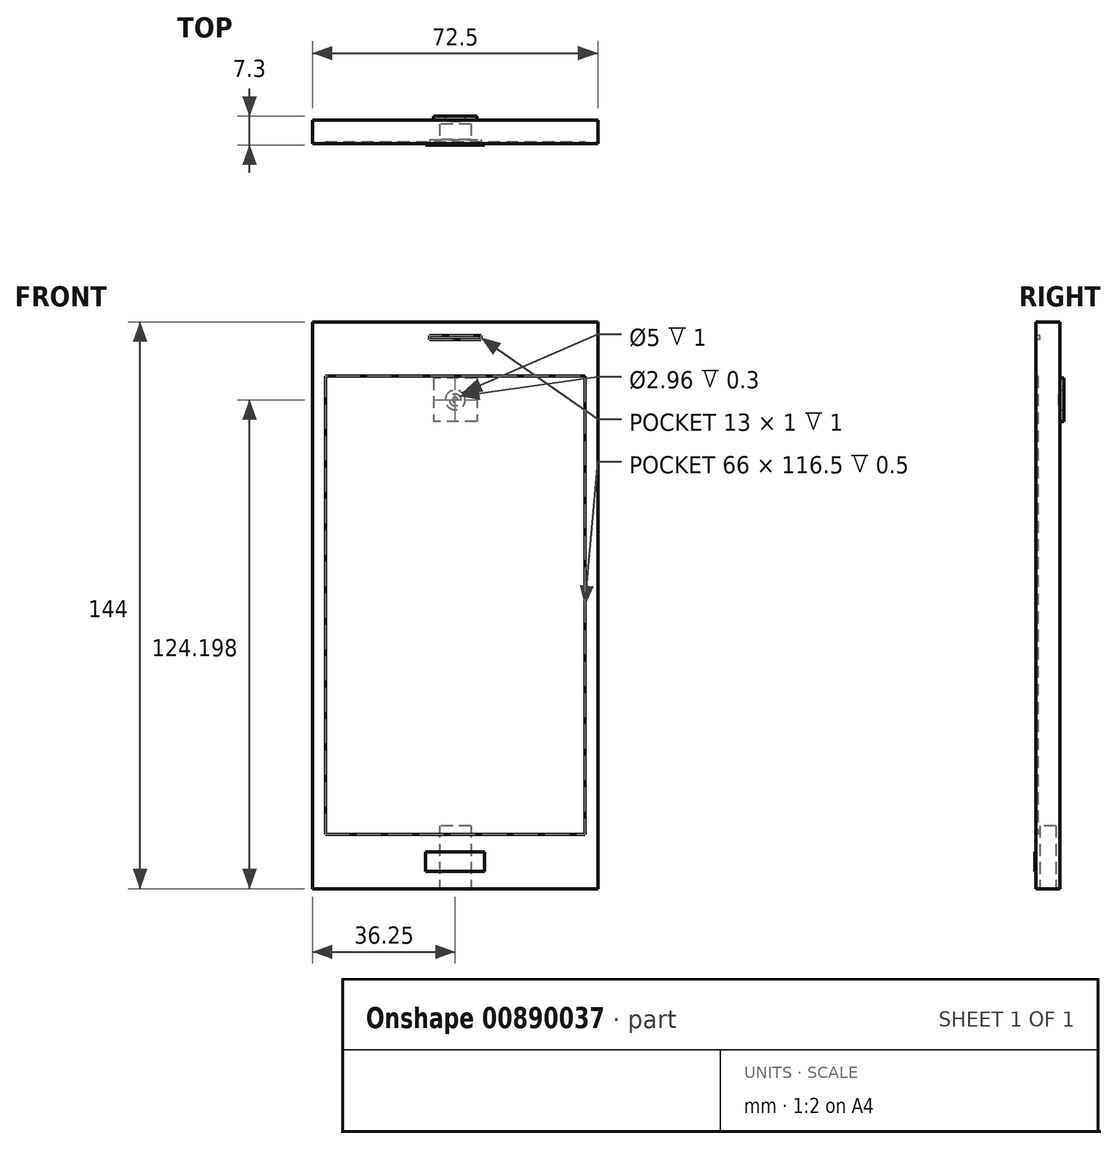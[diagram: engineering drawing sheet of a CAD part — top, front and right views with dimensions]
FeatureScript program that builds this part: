
annotation { "Feature Type Name" : "Feature", "Feature Type Description" : "" }
export const myFeature = defineFeature(function(context is Context, id is Id, definition is map)
    precondition{}
    {
        {
            var Q0;
            Q0=qCreatedBy(makeId("Front.planeOp"),FACE);
            var sketch = newSketch(context, id + "F0", { "sketchPlane" : qUnion([Q0])});
            skLineSegment(sketch, "E0.bottom", {"start": v(-36.25, 72) * mm, "end": v(36.25, 72) * mm});
            skLineSegment(sketch, "E0.top", {"start": v(-36.25, -72) * mm, "end": v(36.25, -72) * mm});
            skLineSegment(sketch, "E0.left", {"start": v(-36.25, 72) * mm, "end": v(-36.25, -72) * mm});
            skLineSegment(sketch, "E0.right", {"start": v(36.25, 72) * mm, "end": v(36.25, -72) * mm});
            skPoint(sketch, "E0.middle", {"position": v(0, 0) * mm});
            skSolve(sketch);
        }
        {
            var Q0;
            Q0=makeQuery(id+"F0.imprint","IMPRINT",FACE,{"disambiguationData":[TD([[makeQuery(id+"F0.imprint","IMPRINT",EDGE,{"derivedFrom":sQuery(id+"F0.wireOp",EDGE,"E0.bottom")}),-1.0]])]});
            extrude(context, id + "F1", {"entities" : qUnion([Q0]), "depth" : 3 * mm, "offsetDistance" : 25.4 * mm});
        }
        {
            var Q0;
            Q0=makeQuery(id+"F1.opExtrude","CAP_FACE",FACE,{"disambiguationData":[OSD([sQuery(id+"F0.wireOp",EDGE,"E0.bottom"),sQuery(id+"F0.wireOp",EDGE,"E0.top"),sQuery(id+"F0.wireOp",EDGE,"E0.left"),sQuery(id+"F0.wireOp",EDGE,"E0.right")])],"isStart":true});
            var sketch = newSketch(context, id + "F2", { "sketchPlane" : qUnion([Q0])});
            skSolve(sketch);
        }
        {
            var Q0;
            Q0=makeQuery(id+"F2.imprint","IMPRINT",FACE,{"disambiguationData":[TD([[makeQuery(id+"F2.imprint","IMPRINT",EDGE,{"derivedFrom":makeQuery(id+"F1.opExtrude","CAP_EDGE",EDGE,{"disambiguationData":[OSD([sQuery(id+"F0.wireOp",EDGE,"E0.bottom")])],"isStart":true})}),1.0]])]});
            extrude(context, id + "F3", {"entities" : qUnion([Q0]), "operationType" : NewBodyOperationType.ADD, "depth" : 3 * mm, "offsetDistance" : 25.4 * mm});
        }
        {
            var Q0;
            Q0=makeQuery(id+"F1.opExtrude","CAP_FACE",FACE,{"disambiguationData":[OSD([sQuery(id+"F0.wireOp",EDGE,"E0.bottom"),sQuery(id+"F0.wireOp",EDGE,"E0.top"),sQuery(id+"F0.wireOp",EDGE,"E0.left"),sQuery(id+"F0.wireOp",EDGE,"E0.right")])],"isStart":false});
            var sketch = newSketch(context, id + "F4", { "sketchPlane" : qUnion([Q0])});
            skLineSegment(sketch, "E1.bottom", {"start": v(-33, 58.25) * mm, "end": v(33, 58.25) * mm});
            skLineSegment(sketch, "E1.top", {"start": v(-33, -58.25) * mm, "end": v(33, -58.25) * mm});
            skLineSegment(sketch, "E1.left", {"start": v(-33, 58.25) * mm, "end": v(-33, -58.25) * mm});
            skLineSegment(sketch, "E1.right", {"start": v(33, 58.25) * mm, "end": v(33, -58.25) * mm});
            skPoint(sketch, "E1.middle", {"position": v(0, 0) * mm});
            skSolve(sketch);
        }
        {
            var Q0;
            Q0=makeQuery(id+"F4.imprint","IMPRINT",FACE,{"disambiguationData":[TD([[makeQuery(id+"F4.imprint","IMPRINT",EDGE,{"derivedFrom":sQuery(id+"F4.wireOp",EDGE,"E1.bottom")}),1.0]])]});
            var sketch = newSketch(context, id + "F5", { "sketchPlane" : qUnion([Q0])});
            skLineSegment(sketch, "E2.bottom", {"start": v(-7.5, -62.63) * mm, "end": v(7.5, -62.63) * mm});
            skLineSegment(sketch, "E2.top", {"start": v(-7.5, -67.63) * mm, "end": v(7.5, -67.63) * mm});
            skLineSegment(sketch, "E2.left", {"start": v(-7.5, -62.63) * mm, "end": v(-7.5, -67.63) * mm});
            skLineSegment(sketch, "E2.right", {"start": v(7.5, -62.63) * mm, "end": v(7.5, -67.63) * mm});
            skPoint(sketch, "E2.middle", {"position": v(0, -65.13) * mm});
            skSolve(sketch);
        }
        {
            var Q0;
            Q0=makeQuery(id+"F5.imprint","IMPRINT",FACE,{"disambiguationData":[TD([[makeQuery(id+"F5.imprint","IMPRINT",EDGE,{"derivedFrom":sQuery(id+"F5.wireOp",EDGE,"E2.bottom")}),-1.0]])]});
            extrude(context, id + "F6", {"entities" : qUnion([Q0]), "operationType" : NewBodyOperationType.ADD, "depth" : .3 * mm, "offsetDistance" : 25.4 * mm});
        }
        {
            var Q0;
            {var subQ0=sQuery(id+"F0.wireOp",EDGE,"E0.top");Q0=makeQuery(id+"F3.boolean.opBoolean","MERGE",FACE,{"derivedFrom":[makeQuery(id+"F1.opExtrude","SWEPT_FACE",FACE,{"disambiguationData":[OSD([subQ0])]}),makeQuery(id+"F3.opExtrude","SWEPT_FACE",FACE,{"disambiguationData":[OSD([subQ0])]})]});}
            var sketch = newSketch(context, id + "F7", { "sketchPlane" : qUnion([Q0])});
            skLineSegment(sketch, "E3.bottom", {"start": v(4, -2) * mm, "end": v(-4, -2) * mm});
            skLineSegment(sketch, "E3.top", {"start": v(4, 2) * mm, "end": v(-4, 2) * mm});
            skLineSegment(sketch, "E3.left", {"start": v(4, -2) * mm, "end": v(4, 2) * mm});
            skLineSegment(sketch, "E3.right", {"start": v(-4, -2) * mm, "end": v(-4, 2) * mm});
            skPoint(sketch, "E3.middle", {"position": v(0, 0) * mm});
            skSolve(sketch);
        }
        {
            var Q0;
            Q0=makeQuery(id+"F7.imprint","IMPRINT",FACE,{"disambiguationData":[TD([[makeQuery(id+"F7.imprint","IMPRINT",EDGE,{"derivedFrom":sQuery(id+"F7.wireOp",EDGE,"E3.bottom")}),-1.0]])]});
            extrude(context, id + "F8", {"entities" : qUnion([Q0]), "operationType" : NewBodyOperationType.REMOVE, "oppositeDirection" : true, "depth" : 16 * mm, "offsetDistance" : 25.4 * mm});
        }
        {
            var Q0;
            Q0=makeQuery(id+"F4.imprint","IMPRINT",FACE,{"disambiguationData":[TD([[makeQuery(id+"F4.imprint","IMPRINT",EDGE,{"derivedFrom":sQuery(id+"F4.wireOp",EDGE,"E1.bottom")}),1.0]])]});
            var sketch = newSketch(context, id + "F9", { "sketchPlane" : qUnion([Q0])});
            skLineSegment(sketch, "E4.bottom", {"start": v(-6.5, 67.58) * mm, "end": v(6.5, 67.58) * mm});
            skLineSegment(sketch, "E4.top", {"start": v(-6.5, 68.58) * mm, "end": v(6.5, 68.58) * mm});
            skLineSegment(sketch, "E4.left", {"start": v(-6.5, 67.58) * mm, "end": v(-6.5, 68.58) * mm});
            skLineSegment(sketch, "E4.right", {"start": v(6.5, 67.58) * mm, "end": v(6.5, 68.58) * mm});
            skPoint(sketch, "E4.middle", {"position": v(0, 68.08) * mm});
            skSolve(sketch);
        }
        {
            var Q0;
            Q0 = qSketchRegion(id + "F9", true);
            extrude(context, id + "F10", {"entities" : qUnion([Q0]), "operationType" : NewBodyOperationType.REMOVE, "oppositeDirection" : true, "depth" : 1 * mm, "offsetDistance" : 25.4 * mm});
        }
        {
            var Q0;
            Q0=makeQuery(id+"F3.opExtrude","CAP_FACE",FACE,{"disambiguationData":[OSD([sQuery(id+"F0.wireOp",EDGE,"E0.bottom"),sQuery(id+"F0.wireOp",EDGE,"E0.top"),sQuery(id+"F0.wireOp",EDGE,"E0.left"),sQuery(id+"F0.wireOp",EDGE,"E0.right")])],"isStart":false});
            var sketch = newSketch(context, id + "F11", { "sketchPlane" : qUnion([Q0])});
            skLineSegment(sketch, "E5.bottom", {"start": v(-5.5, 57.73) * mm, "end": v(5.5, 57.73) * mm});
            skLineSegment(sketch, "E5.top", {"start": v(-5.5, 46.73) * mm, "end": v(5.5, 46.73) * mm});
            skLineSegment(sketch, "E5.left", {"start": v(-5.5, 57.73) * mm, "end": v(-5.5, 46.73) * mm});
            skLineSegment(sketch, "E5.right", {"start": v(5.5, 57.73) * mm, "end": v(5.5, 46.73) * mm});
            skPoint(sketch, "E5.middle", {"position": v(0, 52.23) * mm});
            skSolve(sketch);
        }
        {
            var Q0;
            Q0 = qSketchRegion(id + "F11", true);
            extrude(context, id + "F12", {"entities" : qUnion([Q0]), "operationType" : NewBodyOperationType.ADD, "depth" : 1 * mm, "offsetDistance" : 25.4 * mm});
        }
        {
            var Q0;
            Q0=makeQuery(id+"F12.opExtrude","CAP_FACE",FACE,{"disambiguationData":[OSD([sQuery(id+"F11.wireOp",EDGE,"E5.bottom"),sQuery(id+"F11.wireOp",EDGE,"E5.top"),sQuery(id+"F11.wireOp",EDGE,"E5.left"),sQuery(id+"F11.wireOp",EDGE,"E5.right")])],"isStart":false});
            var sketch = newSketch(context, id + "F13", { "sketchPlane" : qUnion([Q0])});
            skCircle(sketch, "E6", {"center": v(0, 52.2) * mm, "radius": 2.5 * mm});
            skSolve(sketch);
        }
        {
            var Q0;
            Q0=makeQuery(id+"F13.imprint","IMPRINT",FACE,{"disambiguationData":[TD([[makeQuery(id+"F13.imprint","IMPRINT",EDGE,{"derivedFrom":sQuery(id+"F13.wireOp",EDGE,"E6")}),1.0]])]});
            extrude(context, id + "F14", {"entities" : qUnion([Q0]), "operationType" : NewBodyOperationType.REMOVE, "oppositeDirection" : true, "depth" : 1 * mm, "offsetDistance" : 25.4 * mm});
        }
        {
            var Q0;
            Q0=makeQuery(id+"F4.imprint","IMPRINT",FACE,{"disambiguationData":[TD([[makeQuery(id+"F4.imprint","IMPRINT",EDGE,{"derivedFrom":sQuery(id+"F4.wireOp",EDGE,"E1.bottom")}),-1.0]])]});
            extrude(context, id + "F15", {"entities" : qUnion([Q0]), "operationType" : NewBodyOperationType.REMOVE, "oppositeDirection" : true, "depth" : .5 * mm, "offsetDistance" : 25.4 * mm});
        }
        {
            var Q0;
            Q0=makeQuery(id+"F14.boolean.opBoolean","COPY",FACE,{"derivedFrom":makeQuery(id+"F14.opExtrude","CAP_FACE",FACE,{"disambiguationData":[OSD([sQuery(id+"F13.wireOp",EDGE,"E6")])],"isStart":false})});
            var sketch = newSketch(context, id + "F16", { "sketchPlane" : qUnion([Q0])});
            skCircle(sketch, "E7", {"center": v(0, 52.2) * mm, "radius": 1.48 * mm});
            skSolve(sketch);
        }
        {
            var Q0;
            Q0 = qSketchRegion(id + "F16", true);
            extrude(context, id + "F17", {"entities" : qUnion([Q0]), "operationType" : NewBodyOperationType.REMOVE, "oppositeDirection" : true, "depth" : .3 * mm, "offsetDistance" : 25.4 * mm});
        }
        {
            var Q0;
            Q0=makeQuery(id+"F17.boolean.opBoolean","COPY",FACE,{"derivedFrom":makeQuery(id+"F17.opExtrude","CAP_FACE",FACE,{"disambiguationData":[OSD([sQuery(id+"F16.wireOp",EDGE,"E7")])],"isStart":false})});
            var sketch = newSketch(context, id + "F18", { "sketchPlane" : qUnion([Q0])});
            skCircle(sketch, "E8", {"center": v(0, 52.2) * mm, "radius": 0.69 * mm});
            skSolve(sketch);
        }
        {
            var Q0;
            Q0 = qSketchRegion(id + "F18", true);
            extrude(context, id + "F19", {"entities" : qUnion([Q0]), "operationType" : NewBodyOperationType.ADD, "depth" : .1 * mm, "offsetDistance" : 25.4 * mm});
        }
    });
